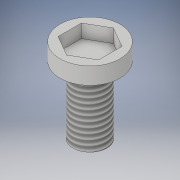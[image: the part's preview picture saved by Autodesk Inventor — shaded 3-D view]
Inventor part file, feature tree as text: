
AUTODESK INVENTOR PART (.ipt)
format: ipt  version: 2017 (Build 210142000, 142)  size: 119,808 bytes
history: native  units: in
note: dims shown in document units (in); Inventor stores cm internally (conversion verified against a paired STEP export)
features: extrude x3, sketch x3, thread x1
ambient origin geometry x8: Origin, YZ Plane, XZ Plane, XY Plane, X Axis, Y Axis, Z Axis, Center Point
bodies: Solid1 (feature_tree)
feature tree (7):
  extrude  "Extrusion1"  Depth=1.0in TaperAngle=0.0deg
  thread  "Thread1"  [1 undecoded]
  extrude  "Extrusion2"  Depth=0.2in TaperAngle=0.0deg
  extrude  "Extrusion3"  [1 undecoded]
  sketch  "Sketch1"  dims[d0=0.5in d1=1.0in d2=0.0in d3=1.0in d4=0.0in]
  sketch  "Sketch2"  dims[d5=0.25in d6=0.0in d7=0.2in d8=0.0in]
  sketch  "Sketch3"
note: 2 required parameter values undecoded (feature->parameter linkage not recoverable at this tier; creation-order binding heuristic only, values carry confidence <= 0.55)
